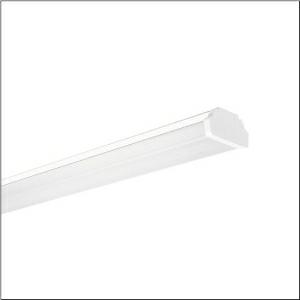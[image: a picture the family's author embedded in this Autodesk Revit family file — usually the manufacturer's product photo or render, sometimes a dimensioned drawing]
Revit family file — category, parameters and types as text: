
# Revit family: dus_r__31_gen_2_53bd812dv6dxd2_e925
name_source: partatom
category: Lighting Fixtures
units: mm (PartAtom-declared; Revit-internal decimal feet)

## family parameters
Cut with Voids When Loaded = No
Host = Face
Light Source = No
Part Type = Normal
Room Calculation Point = No
Round Connector Dimension = Use Diameter
Shared = No

## types (1)
- --- (1 x LED, 13280 lm, 74.9 W, 6500K)
    Apparent Load = 75 VA
    CIE Flux Codes = 47 80 95 93 100
    Color Rendering = 80
    Color Temperature = 6500K
    Default Elevation = 1800 mm
    Description = DUS® 31 Gen.2, luminaire insert, of sheet steel, coil coated, white, length: 1.535mm, width: 81mm, height: 90mm, 5x system unit, system units: 307mm, LED rated luminous flux: 13.280lm, light colour: 865, control gear: DALI 2, control gear: ECG DALI, with plug, 5-pole, with phase selection, mains connection: 220..240V, AC, 50/60Hz, rated input power: 75W, through-wiring accessed according to module size, primary optical cover: cover, of PMMA, light emission: direct distribution, primary light characteristic: symmetric, protection rating (complete): IP20, protection rating (LED compartment): IP50, insulation class (complete): insulation class I (protective earthing), certification: CE, ENEC, VDE, UKCA, impact resistance: IK03, permissible ambient temperature for indoor applications: -25..+35°C, corresponds to IFS (International Featured Standards) requirements for safety and quality in the food industry, reducing of maximum allowable ambient temperature of 5°C with ceiling mounting, packaging unit: 1 piece
    Height = 95 mm
    Lamp = 1 x LED
    Lamp Light Flux = 13280 lm
    Lamp Power = 74.9 W
    Lamp count = 1
    Length = 1535 mm
    Luminous efficacy = 177 lm/W
    Manufacturer = Siteco
    ModVariant = No
    Model = 53BD812DV6DXD2
    Mounting Place = Ceiling
    Mounting Type = Pendant
    Number of Poles = 1
    OnlyDefault = Yes
    Power Factor = 1
    Product Name = DUS® 31 Gen.2
    Product group = luminaire insert | ceiling pendant
    ProductGroupID = 902
    Protection Class = Protection class I
    Protection Degree = IP 20
    RLX_Detail_Level = 1
    RLX_Emergency_Light_Flux = 0 lm
    RLX_Emergency_Type = 0
    RLX_Emergency_Type_DB = No
    RlxData = <blob elided: 32225 chars, md5=0ea2033c>
    Socket = socket
    Standby Power = 0 W
    System Light Flux = 13280 lm
    System Power = 75 W
    Type Comments = factory setting: luminous flux: 100 % | dim-lin: 254 | 511 mA
    Type Image = l_1319596.jpg
    URL = http://relux.com
    VarID = @adj_063141
    Voltage = 0 V
    Weight = 0.00 kg
    Width = 81 mm

## geometry (parser evidence)
native form markers: Blend x4, Sweep x12
no freeform markers — native parametric forms only
